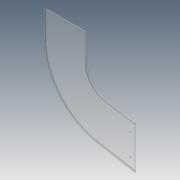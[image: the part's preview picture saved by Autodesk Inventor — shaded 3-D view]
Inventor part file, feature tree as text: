
AUTODESK INVENTOR PART (.ipt)
format: ipt  version: 2012 (Build 160160000, 160)  size: 142,848 bytes
history: native  units: in
note: dims shown in document units (in); Inventor stores cm internally (conversion verified against a paired STEP export)
features: extrude x2, hole x2, pattern_linear x2, sketch x2
ambient origin geometry x8: Origin, YZ Plane, XZ Plane, XY Plane, X Axis, Y Axis, Z Axis, Center Point
bodies: Solid1 (feature_tree)
feature tree (8):
  extrude  "Extrusion1"  Depth=9.625in
  extrude  "Extrusion2"  Depth=5.0in
  hole  "Hole1"  [1 undecoded]
  pattern_linear  "Rectangular Pattern1"  Spacing1=12.5in  [1 undecoded]
  hole  "Hole2"  [1 undecoded]
  pattern_linear  "Rectangular Pattern2"  Spacing1=0.25in  [1 undecoded]
  sketch  "Sketch1"  dims[d0=9.625in d1=9.625in]
  sketch  "Sketch2"  dims[d2=0.6871in d3=5.0in d4=14.625in d5=12.5in d6=20.75in d7=0.25in d8=0.0in d9=0.1875in d10=0.1875in d11=0.1875in d12=0.1875in d13=0.1875in d14=0.1875in d15=0.125in d16=0.125in d17=0.125in d18=0.125in d19=0.125in d20=0.0in d21=1.188in d22=14.875in d23=0.265in d24=0.75in d25=0.375in d26=0.25in d27=0.5635in d28=1.0in d29=0.8108in d30=0.7874in d32=5.0in d33=0.5in d34=1.75in d35=0.265in d36=0.75in d37=0.375in d38=0.25in d39=0.5635in d40=1.0in d41=0.8108in d42=1.1811in d44=3.0in]
note: 4 required parameter values undecoded (feature->parameter linkage not recoverable at this tier; creation-order binding heuristic only, values carry confidence <= 0.55)
